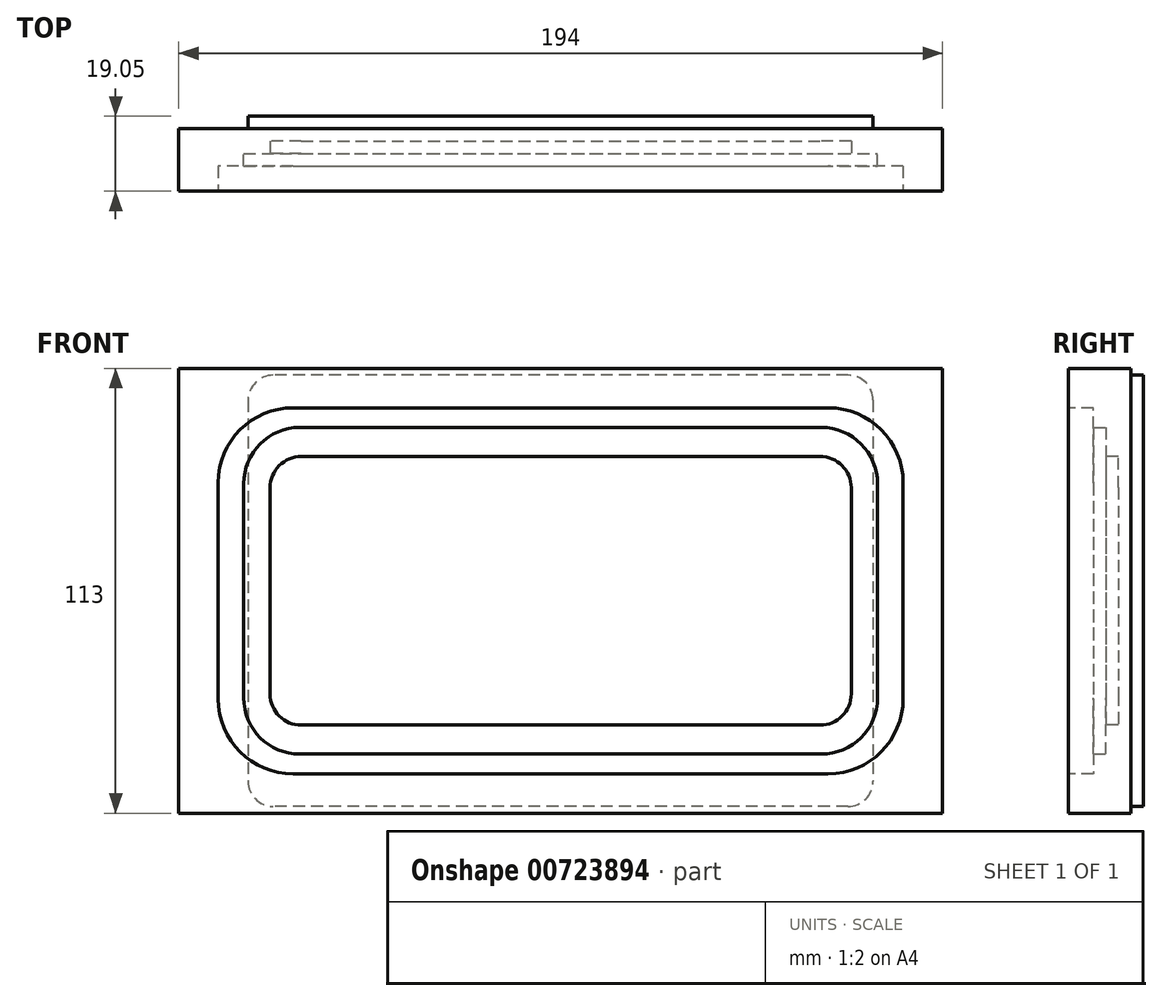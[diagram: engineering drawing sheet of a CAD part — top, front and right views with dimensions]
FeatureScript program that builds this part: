
annotation { "Feature Type Name" : "Feature", "Feature Type Description" : "" }
export const myFeature = defineFeature(function(context is Context, id is Id, definition is map)
    precondition{}
    {
        {
            var Q0;
            Q0=qCreatedBy(makeId("Front.planeOp"),FACE);
            var sketch = newSketch(context, id + "F0", { "sketchPlane" : qUnion([Q0])});
            skLineSegment(sketch, "E0.bottom", {"start": v(73.03, 54.77) * mm, "end": v(-73.03, 54.77) * mm});
            skLineSegment(sketch, "E0.top", {"start": v(73.03, -54.77) * mm, "end": v(-73.02, -54.77) * mm});
            skLineSegment(sketch, "E0.left", {"start": v(79.38, 48.42) * mm, "end": v(79.38, -48.42) * mm});
            skLineSegment(sketch, "E0.right", {"start": v(-79.38, 48.42) * mm, "end": v(-79.37, -48.42) * mm});
            skPoint(sketch, "E0.middle", {"position": v(0, 0) * mm});
            skPoint(sketch, "E1.visualSharp", {"position": v(-79.37, -54.77) * mm});
            skArc(sketch, "E1.filletArc", {"start": v(-79.37, -48.42) * mm, "mid": v(-77.52, -52.9) * mm, "end": v(-73.02, -54.77) * mm});
            skPoint(sketch, "E2.visualSharp", {"position": v(79.38, -54.77) * mm});
            skArc(sketch, "E2.filletArc", {"start": v(73.03, -54.77) * mm, "mid": v(77.52, -52.9) * mm, "end": v(79.38, -48.42) * mm});
            skPoint(sketch, "E3.visualSharp", {"position": v(79.38, 54.77) * mm});
            skArc(sketch, "E3.filletArc", {"start": v(79.38, 48.42) * mm, "mid": v(77.52, 52.9) * mm, "end": v(73.03, 54.77) * mm});
            skPoint(sketch, "E4.visualSharp", {"position": v(-79.38, 54.77) * mm});
            skArc(sketch, "E4.filletArc", {"start": v(-73.03, 54.77) * mm, "mid": v(-77.52, 52.9) * mm, "end": v(-79.38, 48.42) * mm});
            skSolve(sketch);
        }
        {
            var Q0;
            Q0=qSketchRegion(id+"F0",true);
            extrude(context, id + "F1", {"entities" : qUnion([Q0]), "depth" : 3.17 * mm, "offsetDistance" : 25.4 * mm});
        }
        {
            var Q0;
            Q0=makeQuery(id+"F1.opExtrude","CAP_FACE",FACE,{"disambiguationData":[OSD([sQuery(id+"F0.wireOp",EDGE,"E0.bottom"),sQuery(id+"F0.wireOp",EDGE,"E0.top"),sQuery(id+"F0.wireOp",EDGE,"E0.left"),sQuery(id+"F0.wireOp",EDGE,"E0.right")])],"isStart":false});
            var sketch = newSketch(context, id + "F2", { "sketchPlane" : qUnion([Q0])});
            skLineSegment(sketch, "E5.bottom", {"start": v(-97, 56.5) * mm, "end": v(97, 56.5) * mm});
            skLineSegment(sketch, "E5.top", {"start": v(-97, -56.5) * mm, "end": v(97, -56.5) * mm});
            skLineSegment(sketch, "E5.left", {"start": v(-97, 56.5) * mm, "end": v(-97, -56.5) * mm});
            skLineSegment(sketch, "E5.right", {"start": v(97, 56.5) * mm, "end": v(97, -56.5) * mm});
            skPoint(sketch, "E5.middle", {"position": v(0, 0) * mm});
            skSolve(sketch);
        }
        {
            var Q0;
            Q0=qSketchRegion(id+"F2",true);
            extrude(context, id + "F3", {"entities" : qUnion([Q0]), "operationType" : NewBodyOperationType.ADD, "depth" : 15.88 * mm, "offsetDistance" : 25.4 * mm});
        }
        {
            var Q0;
            Q0=makeQuery(id+"F3.opExtrude","CAP_FACE",FACE,{"disambiguationData":[OSD([sQuery(id+"F2.wireOp",EDGE,"E5.bottom"),sQuery(id+"F2.wireOp",EDGE,"E5.top"),sQuery(id+"F2.wireOp",EDGE,"E5.left"),sQuery(id+"F2.wireOp",EDGE,"E5.right")])],"isStart":false});
            var sketch = newSketch(context, id + "F4", { "sketchPlane" : qUnion([Q0])});
            skLineSegment(sketch, "E6.bottom", {"start": v(-67.95, 46.5) * mm, "end": v(67.95, 46.5) * mm});
            skLineSegment(sketch, "E6.top", {"start": v(-67.95, -46.5) * mm, "end": v(67.95, -46.5) * mm});
            skLineSegment(sketch, "E6.left", {"start": v(-87, 27.45) * mm, "end": v(-87, -27.45) * mm});
            skLineSegment(sketch, "E6.right", {"start": v(87, 27.45) * mm, "end": v(87, -27.45) * mm});
            skPoint(sketch, "E6.middle", {"position": v(0, 0) * mm});
            skPoint(sketch, "E7.visualSharp", {"position": v(-87, 46.5) * mm});
            skArc(sketch, "E7.filletArc", {"start": v(-67.95, 46.5) * mm, "mid": v(-81.42, 40.92) * mm, "end": v(-87, 27.45) * mm});
            skPoint(sketch, "E8.visualSharp", {"position": v(87, 46.5) * mm});
            skArc(sketch, "E8.filletArc", {"start": v(87, 27.45) * mm, "mid": v(81.42, 40.92) * mm, "end": v(67.95, 46.5) * mm});
            skPoint(sketch, "E9.visualSharp", {"position": v(87, -46.5) * mm});
            skArc(sketch, "E9.filletArc", {"start": v(67.95, -46.5) * mm, "mid": v(81.42, -40.92) * mm, "end": v(87, -27.45) * mm});
            skPoint(sketch, "E10.visualSharp", {"position": v(-87, -46.5) * mm});
            skArc(sketch, "E10.filletArc", {"start": v(-87, -27.45) * mm, "mid": v(-81.42, -40.92) * mm, "end": v(-67.95, -46.5) * mm});
            skSolve(sketch);
        }
        {
            var Q0;
            Q0=makeQuery(id+"F4.imprint","IMPRINT",FACE,{"disambiguationData":[TD([[makeQuery(id+"F4.imprint","IMPRINT",EDGE,{"derivedFrom":sQuery(id+"F4.wireOp",EDGE,"E6.bottom")}),-1.0]])]});
            extrude(context, id + "F5", {"entities" : qUnion([Q0]), "operationType" : NewBodyOperationType.REMOVE, "oppositeDirection" : true, "depth" : 12.7 * mm, "offsetDistance" : 25.4 * mm});
        }
        {
            var Q0;
            Q0=makeQuery(id+"F5.boolean.opBoolean","COPY",FACE,{"derivedFrom":makeQuery(id+"F5.opExtrude","CAP_FACE",FACE,{"disambiguationData":[OSD([sQuery(id+"F4.wireOp",EDGE,"E6.bottom"),sQuery(id+"F4.wireOp",EDGE,"E6.top"),sQuery(id+"F4.wireOp",EDGE,"E6.left"),sQuery(id+"F4.wireOp",EDGE,"E6.right"),sQuery(id+"F4.wireOp",EDGE,"E7.filletArc"),sQuery(id+"F4.wireOp",EDGE,"E8.filletArc"),sQuery(id+"F4.wireOp",EDGE,"E9.filletArc"),sQuery(id+"F4.wireOp",EDGE,"E10.filletArc")])],"isStart":false})});
            var sketch = newSketch(context, id + "F6", { "sketchPlane" : qUnion([Q0])});
            skLineSegment(sketch, "E11.bottom", {"start": v(-66.21, 41.5) * mm, "end": v(66.21, 41.5) * mm});
            skLineSegment(sketch, "E11.top", {"start": v(-66.21, -41.5) * mm, "end": v(66.21, -41.5) * mm});
            skLineSegment(sketch, "E11.left", {"start": v(-80.5, 27.21) * mm, "end": v(-80.5, -27.21) * mm});
            skLineSegment(sketch, "E11.right", {"start": v(80.5, 27.21) * mm, "end": v(80.5, -27.21) * mm});
            skPoint(sketch, "E11.middle", {"position": v(0, 0) * mm});
            skPoint(sketch, "E12.visualSharp", {"position": v(-80.5, 41.5) * mm});
            skArc(sketch, "E12.filletArc", {"start": v(-66.21, 41.5) * mm, "mid": v(-76.32, 37.32) * mm, "end": v(-80.5, 27.21) * mm});
            skPoint(sketch, "E13.visualSharp", {"position": v(80.5, 41.5) * mm});
            skArc(sketch, "E13.filletArc", {"start": v(80.5, 27.21) * mm, "mid": v(76.32, 37.32) * mm, "end": v(66.21, 41.5) * mm});
            skPoint(sketch, "E14.visualSharp", {"position": v(80.5, -41.5) * mm});
            skArc(sketch, "E14.filletArc", {"start": v(66.21, -41.5) * mm, "mid": v(76.32, -37.32) * mm, "end": v(80.5, -27.21) * mm});
            skPoint(sketch, "E15.visualSharp", {"position": v(-80.5, -41.5) * mm});
            skArc(sketch, "E15.filletArc", {"start": v(-80.5, -27.21) * mm, "mid": v(-76.32, -37.32) * mm, "end": v(-66.21, -41.5) * mm});
            skSolve(sketch);
        }
        {
            var Q0;
            Q0=makeQuery(id+"F6.imprint","IMPRINT",FACE,{"disambiguationData":[TD([[makeQuery(id+"F6.imprint","IMPRINT",EDGE,{"derivedFrom":sQuery(id+"F6.wireOp",EDGE,"E11.bottom")}),-1.0]])]});
            extrude(context, id + "F7", {"entities" : qUnion([Q0]), "operationType" : NewBodyOperationType.ADD, "depth" : 3.17 * mm, "offsetDistance" : 25.4 * mm});
        }
        {
            var Q0;
            Q0=makeQuery(id+"F7.opExtrude","CAP_FACE",FACE,{"disambiguationData":[OSD([sQuery(id+"F6.wireOp",EDGE,"E11.bottom"),sQuery(id+"F6.wireOp",EDGE,"E11.top"),sQuery(id+"F6.wireOp",EDGE,"E11.left"),sQuery(id+"F6.wireOp",EDGE,"E11.right"),sQuery(id+"F6.wireOp",EDGE,"E12.filletArc"),sQuery(id+"F6.wireOp",EDGE,"E13.filletArc"),sQuery(id+"F6.wireOp",EDGE,"E14.filletArc"),sQuery(id+"F6.wireOp",EDGE,"E15.filletArc")])],"isStart":false});
            var sketch = newSketch(context, id + "F8", { "sketchPlane" : qUnion([Q0])});
            skLineSegment(sketch, "E16.bottom", {"start": v(-65.88, 34.13) * mm, "end": v(65.88, 34.13) * mm});
            skLineSegment(sketch, "E16.top", {"start": v(-65.88, -34.13) * mm, "end": v(65.88, -34.13) * mm});
            skLineSegment(sketch, "E16.left", {"start": v(-73.82, 26.2) * mm, "end": v(-73.82, -26.2) * mm});
            skLineSegment(sketch, "E16.right", {"start": v(73.82, 26.2) * mm, "end": v(73.82, -26.2) * mm});
            skPoint(sketch, "E16.middle", {"position": v(0, 0) * mm});
            skPoint(sketch, "E17.visualSharp", {"position": v(-73.82, 34.13) * mm});
            skArc(sketch, "E17.filletArc", {"start": v(-65.88, 34.13) * mm, "mid": v(-71.5, 31.8) * mm, "end": v(-73.82, 26.2) * mm});
            skPoint(sketch, "E18.visualSharp", {"position": v(73.82, 34.13) * mm});
            skArc(sketch, "E18.filletArc", {"start": v(73.82, 26.2) * mm, "mid": v(71.5, 31.8) * mm, "end": v(65.88, 34.13) * mm});
            skPoint(sketch, "E19.visualSharp", {"position": v(73.82, -34.13) * mm});
            skArc(sketch, "E19.filletArc", {"start": v(65.88, -34.13) * mm, "mid": v(71.5, -31.8) * mm, "end": v(73.82, -26.2) * mm});
            skPoint(sketch, "E20.visualSharp", {"position": v(-73.82, -34.13) * mm});
            skArc(sketch, "E20.filletArc", {"start": v(-73.82, -26.2) * mm, "mid": v(-71.5, -31.8) * mm, "end": v(-65.88, -34.13) * mm});
            skSolve(sketch);
        }
        {
            var Q0;
            Q0=makeQuery(id+"F8.imprint","IMPRINT",FACE,{"disambiguationData":[TD([[makeQuery(id+"F8.imprint","IMPRINT",EDGE,{"derivedFrom":sQuery(id+"F8.wireOp",EDGE,"E16.bottom")}),-1.0]])]});
            extrude(context, id + "F9", {"entities" : qUnion([Q0]), "operationType" : NewBodyOperationType.REMOVE, "oppositeDirection" : true, "depth" : 3.17 * mm, "offsetDistance" : 25.4 * mm});
        }
        {
            var Q0;
            Q0=makeQuery(id+"F5.boolean.opBoolean","COPY",FACE,{"derivedFrom":makeQuery(id+"F5.opExtrude","CAP_FACE",FACE,{"disambiguationData":[OSD([sQuery(id+"F4.wireOp",EDGE,"E6.bottom"),sQuery(id+"F4.wireOp",EDGE,"E6.top"),sQuery(id+"F4.wireOp",EDGE,"E6.left"),sQuery(id+"F4.wireOp",EDGE,"E6.right"),sQuery(id+"F4.wireOp",EDGE,"E7.filletArc"),sQuery(id+"F4.wireOp",EDGE,"E8.filletArc"),sQuery(id+"F4.wireOp",EDGE,"E9.filletArc"),sQuery(id+"F4.wireOp",EDGE,"E10.filletArc")])],"isStart":false})});
            extrude(context, id + "F10", {"entities" : qUnion([Q0]), "operationType" : NewBodyOperationType.ADD, "depth" : 6.35 * mm, "offsetDistance" : 25.4 * mm});
        }
    });
